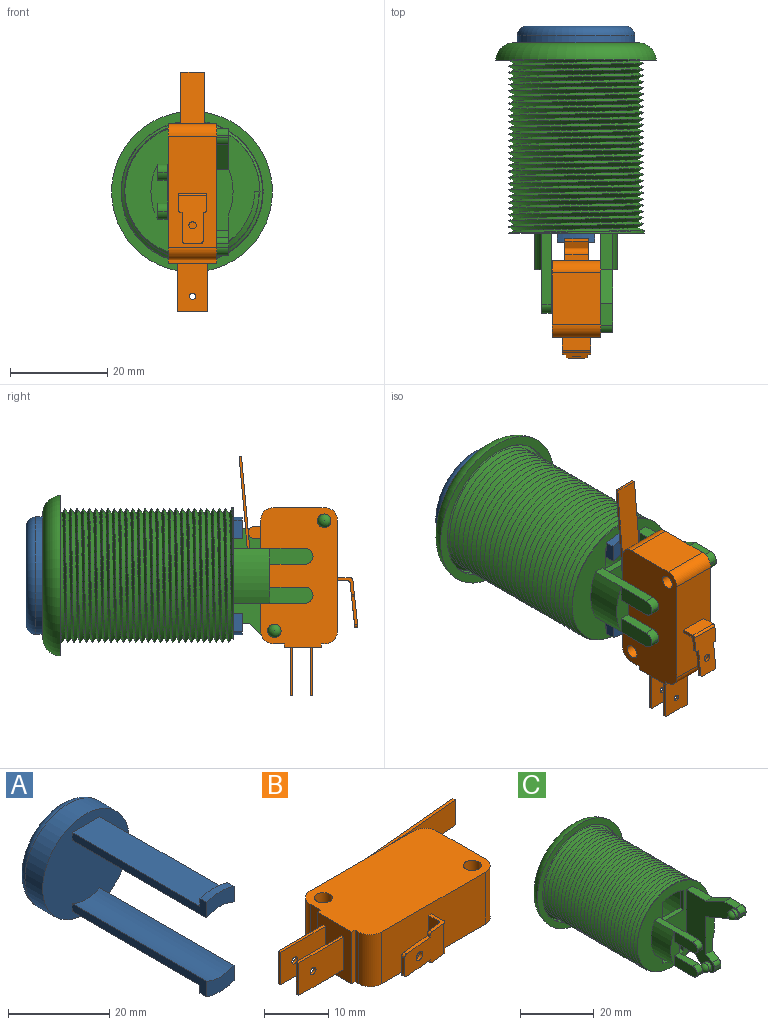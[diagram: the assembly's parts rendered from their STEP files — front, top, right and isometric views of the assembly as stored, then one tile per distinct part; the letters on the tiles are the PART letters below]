
ASSEMBLY  parts=3 mates=2
PART A: 18 faces, bbox 26.1x45.6x26.1 mm
  f0: plane 24.13x24.13mm, normal (0,-1,0), area 437.9mm2, adj f1,f5,f6,f7,f10,f11,f12,f14
  f1: cylinder r=12.06mm len=24.13mm, axis (0,-1,0), area 373.5mm2, adj f0,f3
  f2: sphere r=37.39mm, area 291.6mm2, adj f3
  f3: torus R=10.06mm, axis (0,1,0), area 255.7mm2, adj f1,f2
  f4: cylinder r=12.06mm len=7.7mm, axis (0,1,0), area 13.9mm2, adj f5,f7,f8,f17
  f5: plane 37.5x3.78mm, normal (1,0,0), area 73.4mm2, adj f0,f4,f6,f8,f16,f17
  f6: cylinder r=8.56mm len=37.5mm, axis (0,1,0), area 299.5mm2, adj f0,f5,f7,f8
  f7: plane 37.5x3.78mm, normal (-1,0,0), area 73.4mm2, adj f0,f4,f6,f8,f16,f17
  f8: plane 7.7x4.42mm, normal (0,-1,0), area 27.6mm2, adj f4,f5,f6,f7
  f9: cylinder r=12.06mm len=7.7mm, axis (0,1,0), area 13.9mm2, adj f10,f12,f13,f15
  f10: plane 37.5x3.78mm, normal (-1,0,0), area 74.4mm2, adj f0,f9,f11,f13,f14,f15
  f11: cylinder r=8.56mm len=37.5mm, axis (0,1,0), area 299.5mm2, adj f0,f10,f12,f13
  f12: plane 37.5x3.78mm, normal (1,0,0), area 74.4mm2, adj f0,f9,f11,f13,f14,f15
  f13: plane 7.7x4.42mm, normal (0,-1,0), area 27.6mm2, adj f9,f10,f11,f12
  f14: plane 35.66x7.7mm, normal (0,0,1), area 274.6mm2, adj f0,f10,f12,f15
  f15: plane 7.7x2.52mm, normal (0,1,0.03), area 17.8mm2, adj f9,f10,f12,f14
  f16: plane 35.66x7.7mm, normal (0,0,-1), area 274.6mm2, adj f0,f5,f7,f17
  f17: plane 7.7x2.55mm, normal (0,1,-0.03), area 18mm2, adj f4,f5,f7,f16
PART B: 60 faces, bbox 49.2x24.4x9.9 mm
  f0: cylinder r=0.51mm len=0.69mm, axis (-0.11,0.99,0), area 0.5mm2, adj f3,f4,f49,f56
  f1: cylinder r=0.51mm len=5.84mm, axis (0,0,-1), area 4.3mm2, adj f4,f49,f50,f52
  f2: cylinder r=0.51mm len=0.69mm, axis (0.11,-0.99,0), area 0.5mm2, adj f3,f4,f50,f53
  f3: plane 9.71x5.84mm, normal (0.11,-0.99,0), area 45.3mm2, adj f0,f2,f41,f42,f43,f48,f49,f50
  f4: plane 9.14x5.84mm, normal (-0.11,0.99,0), area 42mm2, adj f0,f1,f2,f41,f42,f48,f49,f50
  f5: plane 2.54x2.54mm, normal (0,0,1), area 5.7mm2, adj f7,f8,f9,f38
  f6: plane 2.54x2.54mm, normal (0,0,-1), area 5.7mm2, adj f7,f8,f9,f38
  f7: plane 4.83x1.27mm, normal (-1,0,0), area 6.1mm2, adj f5,f6,f8,f38
  f8: cylinder r=1.27mm len=4.83mm, axis (0,0,1), area 19.3mm2, adj f5,f6,f7,f9
  f9: plane 4.83x1.27mm, normal (1,0,0), area 6.1mm2, adj f5,f6,f8,f38
  f10: plane 27.59x4.45mm, normal (0,0,1), area 14.8mm2, adj f12,f13,f14,f15,f16,f38,f44,f45
  f11: plane 27.59x4.45mm, normal (0,0,-1), area 14.8mm2, adj f12,f13,f14,f15,f16,f38,f44,f45
  f12: plane 4.83x0.51mm, normal (1,0.09,0), area 2.5mm2, adj f10,f11,f13,f16
  f13: plane 26.62x4.83mm, normal (0.09,-1,0), area 129.1mm2, adj f10,f11,f12,f44
  f14: plane 4.83x1.06mm, normal (1,0,0), area 5.1mm2, adj f10,f11,f38,f44
  f15: plane 4.83x1.52mm, normal (-1,0,0), area 7.4mm2, adj f10,f11,f38,f45
  f16: plane 27.08x4.83mm, normal (-0.09,1,0), area 131.3mm2, adj f10,f11,f12,f45
  f17: plane 9.91x0.51mm, normal (0,0,1), area 5mm2, adj f19,f20,f21,f34
  f18: plane 9.91x0.51mm, normal (0,0,-1), area 5mm2, adj f19,f20,f21,f34
  f19: plane 9.91x6.21mm, normal (0,1,0), area 60.2mm2, adj f17,f18,f21,f34,f47
  f20: plane 9.91x6.21mm, normal (0,-1,0), area 60.2mm2, adj f17,f18,f21,f34,f47
  f21: plane 6.21x0.51mm, normal (-1,0,0), area 3.2mm2, adj f17,f18,f19,f20
  f22: plane 9.91x0.51mm, normal (0,0,1), area 5mm2, adj f24,f25,f26,f34
  f23: plane 9.91x0.51mm, normal (0,0,-1), area 5mm2, adj f24,f25,f26,f34
  f24: plane 9.91x6.21mm, normal (0,1,0), area 60.2mm2, adj f22,f23,f26,f34,f46
  f25: plane 9.91x6.21mm, normal (0,-1,0), area 60.2mm2, adj f22,f23,f26,f34,f46
  f26: plane 6.21x0.51mm, normal (-1,0,0), area 3.2mm2, adj f22,f23,f24,f25
  f27: plane 28.7x15.75mm, normal (0,0,1), area 428mm2, adj f29,f30,f31,f32,f33,f34,f35,f36
  f28: plane 28.7x15.75mm, normal (0,0,-1), area 428mm2, adj f29,f30,f31,f32,f33,f34,f35,f36
  f29: cylinder r=2.54mm len=9.91mm, axis (0,0,1), area 39.5mm2, adj f27,f28,f30,f40
  f30: plane 22.86x9.91mm, normal (0,-1,0), area 222.8mm2, adj f27,f28,f29,f31,f49,f50,f51,f52
  f31: cylinder r=2.54mm len=9.91mm, axis (0,0,1), area 39.5mm2, adj f27,f28,f30,f32
  f32: plane 9.91x0.76mm, normal (-1,0,0), area 7.6mm2, adj f27,f28,f31,f33
  f33: plane 9.91x0.76mm, normal (0,-1,0), area 7.6mm2, adj f27,f28,f32,f34
  f34: plane 9.91x7.62mm, normal (-1,0,0), area 69.2mm2, adj f17,f18,f19,f20,f22,f23,f24,f25
  f35: plane 9.91x0.76mm, normal (0,1,0), area 7.6mm2, adj f27,f28,f34,f36
  f36: plane 9.91x2.29mm, normal (-1,0,0), area 22.7mm2, adj f27,f28,f35,f37
  f37: cylinder r=2.54mm len=9.91mm, axis (0,0,1), area 39.5mm2, adj f27,f28,f36,f38
  f38: plane 22.86x9.91mm, normal (0,1,0), area 211.8mm2, adj f5,f6,f7,f9,f10,f11,f14,f15
  f39: cylinder r=2.54mm len=9.91mm, axis (0,0,1), area 39.5mm2, adj f27,f28,f38,f40
  f40: plane 10.67x9.91mm, normal (1,0,0), area 105.7mm2, adj f27,f28,f29,f39
  f41: cylinder r=0.51mm len=0.69mm, axis (0.11,-0.99,0), area 0.5mm2, adj f3,f4,f48,f55
  f42: cylinder r=0.51mm len=0.69mm, axis (0.11,-0.99,0), area 0.5mm2, adj f3,f4,f48,f54
  f43: cylinder r=0.51mm len=5.84mm, axis (0,0,1), area 4.3mm2, adj f3,f49,f50,f51
  f44: cylinder r=0.51mm len=4.83mm, axis (0,0,-1), area 3.6mm2, adj f10,f11,f13,f14
  f45: cylinder r=0.51mm len=4.83mm, axis (0,0,1), area 3.6mm2, adj f10,f11,f15,f16
  f46: cylinder r=0.64mm len=1.27mm, axis (0,1,0), area 2mm2, adj f24,f25
  f47: cylinder r=0.64mm len=1.27mm, axis (0,1,0), area 2mm2, adj f19,f20
  f48: plane 3.3x0.63mm, normal (-0.99,-0.11,0), area 2.1mm2, adj f3,f4,f41,f42
  f49: plane 3.47x3.41mm, normal (0,0,-1), area 3.7mm2, adj f0,f1,f3,f4,f30,f43,f51,f52
  f50: plane 3.47x3.41mm, normal (0,0,1), area 3.7mm2, adj f1,f2,f3,f4,f30,f43,f51,f52
  f51: plane 5.84x2.65mm, normal (1,0,0), area 15.5mm2, adj f30,f43,f49,f50
  f52: plane 5.84x2.08mm, normal (-1,0,0), area 12.2mm2, adj f1,f30,f49,f50
  f53: plane 0.63x0.25mm, normal (-0.99,-0.11,0), area 0.2mm2, adj f2,f3,f4,f54
  f54: plane 5.88x1.26mm, normal (0,0,1), area 3.7mm2, adj f3,f4,f42,f53
  f55: plane 5.88x1.26mm, normal (0,0,-1), area 3.7mm2, adj f3,f4,f41,f56
  f56: plane 0.63x0.25mm, normal (-0.99,-0.11,0), area 0.2mm2, adj f0,f3,f4,f55
  f57: cylinder r=0.76mm len=1.58mm, axis (-0.11,0.99,0), area 3mm2, adj f3,f4
  f58: cylinder r=1.4mm len=9.91mm, axis (0,0,-1), area 86.9mm2, adj f27,f28
  f59: cylinder r=1.4mm len=9.91mm, axis (0,0,-1), area 86.9mm2, adj f27,f28
PART C: 64 faces, bbox 36.6x60.3x36.6 mm
  f0: plane 20.4x8.44mm, normal (1,0,0), area 100.3mm2, adj f5,f6,f34,f36,f51,f52,f55,f58
  f1: plane 11.35x3.36mm, normal (0,-1,0), area 19.7mm2, adj f3,f31,f41,f42,f45,f46
  f2: plane 7.5x0mm, normal (1,0,0), area 0mm2, adj f32,f44
  f3: plane 16.4x8mm, normal (1,0,0), area 88.5mm2, adj f1,f5,f30,f42,f44,f49,f50
  f4: plane 26x20.4mm, normal (-1,0,0), area 217.2mm2, adj f5,f7,f34,f35,f36,f37,f39,f51
  f5: plane 28.6x27.92mm, normal (0,-1,0), area 378.4mm2, adj f0,f3,f4,f6,f14,f15,f16,f17
  f6: cylinder r=12.52mm len=9.12mm, axis (0,1,0), area 70mm2, adj f0,f5,f7,f33
  f7: plane 12.49x3.36mm, normal (0,-1,0), area 36.5mm2, adj f4,f6,f33,f53,f55
  f8: plane 33.15x33.15mm, normal (0,-1,0), area 186.5mm2, adj f10,f11,f12,f13
  f9: plane 25.42x25.42mm, normal (0,1,0), area 20.7mm2, adj f10,f20
  f10: torus R=12.71mm, axis (0,-1,0), area 542.7mm2, adj f8,f9
  f11: plane 1.86x1.77mm, normal (0.31,0,-0.95), area 1.7mm2, adj f8,f12,f13,f16,f17,f18
  f12: bspline ~29.14x29.14mm, area 73.6mm2, adj f8,f11,f13,f18
  f13: bspline ~29.33x29.33mm, area 26.7mm2, adj f8,f11,f12
  f14: plane 1.1x0.65mm, normal (0,0,-1), area 0.4mm2, adj f5,f15,f17,f19
  f15: bspline ~27.98x19.88mm, area 8.2mm2, adj f5,f14,f16,f19
  f16: bspline ~36.7x27.59mm, area 2815.8mm2, adj f5,f11,f15,f17
  f17: bspline ~36.96x27.59mm, area 3151.4mm2, adj f5,f11,f14,f16,f18
  f18: bspline ~31.31x31.31mm, area 77.3mm2, adj f11,f12,f17
  f19: cylinder r=13.97mm len=27.22mm, axis (0,1,0), area 11.2mm2, adj f5,f14,f15
  f20: cylinder r=12.45mm len=37.7mm, axis (0,1,0), area 2948.3mm2, adj f9,f21
  f21: plane 24.89x24.89mm, normal (0,1,0), area 372.9mm2, adj f20,f22,f23,f24,f25,f26,f27,f28
  f22: cylinder r=10.92mm len=8.15mm, axis (0,-1,0), area 11.8mm2, adj f5,f21,f23,f25
  f23: plane 6.45x1.41mm, normal (-1,0,0), area 9.1mm2, adj f5,f21,f22,f24
  f24: plane 8.15x1.41mm, normal (0,0,1), area 11.5mm2, adj f5,f21,f23,f25
  f25: plane 6.45x1.41mm, normal (1,0,0), area 9.1mm2, adj f5,f21,f22,f24
  f26: plane 6.45x1.41mm, normal (-1,0,0), area 9.1mm2, adj f5,f21,f27,f29
  f27: cylinder r=10.92mm len=8.15mm, axis (0,-1,0), area 11.8mm2, adj f5,f21,f26,f28
  f28: plane 6.45x1.41mm, normal (1,0,0), area 9.1mm2, adj f5,f21,f27,f29
  f29: plane 8.15x1.41mm, normal (0,0,-1), area 11.5mm2, adj f5,f21,f26,f28
  f30: plane 14.65x2mm, normal (0,0,1), area 29.3mm2, adj f3,f5,f31,f41,f49
  f31: cylinder r=12.52mm len=11.35mm, axis (0,1,0), area 88.3mm2, adj f1,f5,f30,f32
  f32: plane 7.5x2mm, normal (0,0,-1), area 15mm2, adj f2,f5,f31,f43
  f33: plane 10.75x8.44mm, normal (1,0,0), area 60.2mm2, adj f5,f6,f7,f35,f53,f54,f56,f57
  f34: plane 4.49x2.5mm, normal (0,0,1), area 11.2mm2, adj f0,f4,f52,f58
  f35: plane 2.86x2.5mm, normal (0,0,-1), area 7.2mm2, adj f4,f33,f57,f61
  f36: plane 2.5x0.43mm, normal (0,-1,0), area 1.1mm2, adj f0,f4,f58,f59
  f37: cylinder r=1.37mm len=2.73mm, axis (1,0,0), area 9.8mm2, adj f4,f63
  f38: plane 0.01x0.01mm, normal (-1,0,0), area 0mm2, adj f63
  f39: cylinder r=1.37mm len=2.73mm, axis (1,0,0), area 9.8mm2, adj f4,f62
  f40: plane 0.01x0.01mm, normal (-1,0,0), area 0mm2, adj f62
  f41: plane 8.9x3.35mm, normal (-1,0,0), area 28.5mm2, adj f1,f30,f42,f49,f50
  f42: plane 7.15x2mm, normal (0,0,-1), area 14.3mm2, adj f1,f3,f41,f50
  f43: plane 7.15x2mm, normal (0,0,-1), area 14.3mm2, adj f32,f44,f46,f48
  f44: plane 16.4x3.35mm, normal (1,0,0), area 53.6mm2, adj f2,f3,f5,f43,f45,f47,f48
  f45: plane 7.15x2mm, normal (0,0,1), area 14.3mm2, adj f1,f44,f46,f47
  f46: plane 8.9x3.35mm, normal (-1,0,0), area 28.5mm2, adj f1,f43,f45,f47,f48
  f47: cylinder r=1.75mm len=2mm, axis (-1,0,0), area 5.3mm2, adj f44,f45,f46,f48
  f48: cylinder r=1.75mm len=2mm, axis (1,0,0), area 5.3mm2, adj f43,f44,f46,f47
  f49: cylinder r=1.75mm len=2mm, axis (-1,0,0), area 5.3mm2, adj f3,f30,f41,f50
  f50: cylinder r=1.75mm len=2mm, axis (1,0,0), area 5.3mm2, adj f3,f41,f42,f49
  f51: plane 7.5x2.5mm, normal (0,0,1), area 18.8mm2, adj f0,f4,f5,f52
  f52: plane 6.91x3.25mm, normal (0,0.43,0.9), area 19.1mm2, adj f0,f4,f34,f51
  f53: plane 2.52x2.5mm, normal (0,-0.51,0.86), area 7.3mm2, adj f4,f7,f33,f60
  f54: plane 2.5x0.78mm, normal (0,-1,0), area 1.9mm2, adj f4,f33,f60,f61
  f55: plane 11.99x5.13mm, normal (0,-0.39,-0.92), area 32.6mm2, adj f0,f4,f7,f59
  f56: plane 3.33x2.5mm, normal (0,0,-1), area 8.3mm2, adj f4,f5,f33,f57
  f57: plane 3.25x3.06mm, normal (0,0.73,-0.69), area 11.2mm2, adj f4,f33,f35,f56
  f58: cylinder r=1.5mm len=2.5mm, axis (-1,0,0), area 5.9mm2, adj f0,f4,f34,f36
  f59: cylinder r=1.5mm len=2.5mm, axis (1,0,0), area 4.4mm2, adj f0,f4,f36,f55
  f60: cylinder r=1.5mm len=2.5mm, axis (1,0,0), area 3.9mm2, adj f4,f33,f53,f54
  f61: cylinder r=1.5mm len=2.5mm, axis (1,0,0), area 5.9mm2, adj f4,f33,f35,f54
  f62: torus R=0.01mm, axis (-1,0,0), area 11.7mm2, adj f39,f40
  f63: torus R=0.01mm, axis (-1,0,0), area 11.7mm2, adj f37,f38
PLACE A t=(-0.6,2.07,3.75)mm
PLACE B rot(axis=(0,-1,0),90deg) t=(-0.48,-47.07,3.74)mm
PLACE C t=(-0.6,2.01,3.75)mm
MATE fastened B.f59 <-> C.f39  axis (1,0,0) through (4.47,-52.23,15.04)mm
MATE fastened A.f1 <-> C.f10  axis (0,-1,0) through (-0.6,2.07,3.75)mm
